# Revit family: 2 posti con tavolino destro - 7802 -
name_source: partatom
category: Furniture
units: mm (PartAtom-declared; Revit-internal decimal feet)

## family parameters
Always vertical = Yes
Cut with Voids When Loaded = No
OmniClass Number = 23.40.20.00
OmniClass Title = General Furniture and Specialties
Room Calculation Point = No
Shared = No
Work Plane-Based = No

## types (1)
- 2 posti con tavolino destro - 7802 -
    Default Elevation = 0 cm
    Description = Two-seater sofa with a metal and wood frame and powdercoated aluminium T-leg, fitted with a right-side table made of plywood with a reconstituted oak or walnut finish. External structure and inner cushions upholstered in fabric, leather, coated fabric or customer’s own material. The seat and back cushions have removable upholstery. The frame upholstery can be  separated and replaced by technical personnel, since it is applied without the use of glue.
    Keynote = sofa
    Manufacturer = ARPER s.p.a.
    Model = Steeve Lou
    URL = http://www.arper.com
